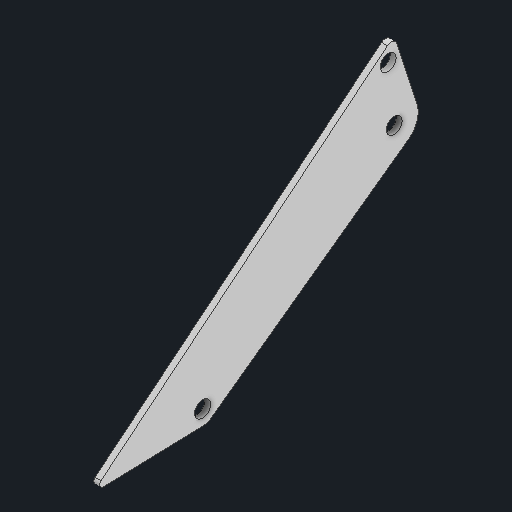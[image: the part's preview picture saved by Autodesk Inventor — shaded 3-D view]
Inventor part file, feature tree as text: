
AUTODESK INVENTOR PART (.ipt)
format: ipt  version: 2025 (Build 290162000, 162)  size: 100,352 bytes
history: native  units: in
note: dims shown in document units (in); Inventor stores cm internally (conversion verified against a paired STEP export)
features: extrude x1, sketch x1
ambient origin geometry x8: Origin, YZ Plane, XZ Plane, XY Plane, X Axis, Y Axis, Z Axis, Center Point
bodies: Solid1 (feature_tree)
feature tree (2):
  extrude  "Extrusion1"  Depth=0.0625in TaperAngle=0.0deg
  sketch  "Sketch1"  dims[d1=0.5in d2=0.164in d3=0.0625in d4=0.0in d5=0.164in]
